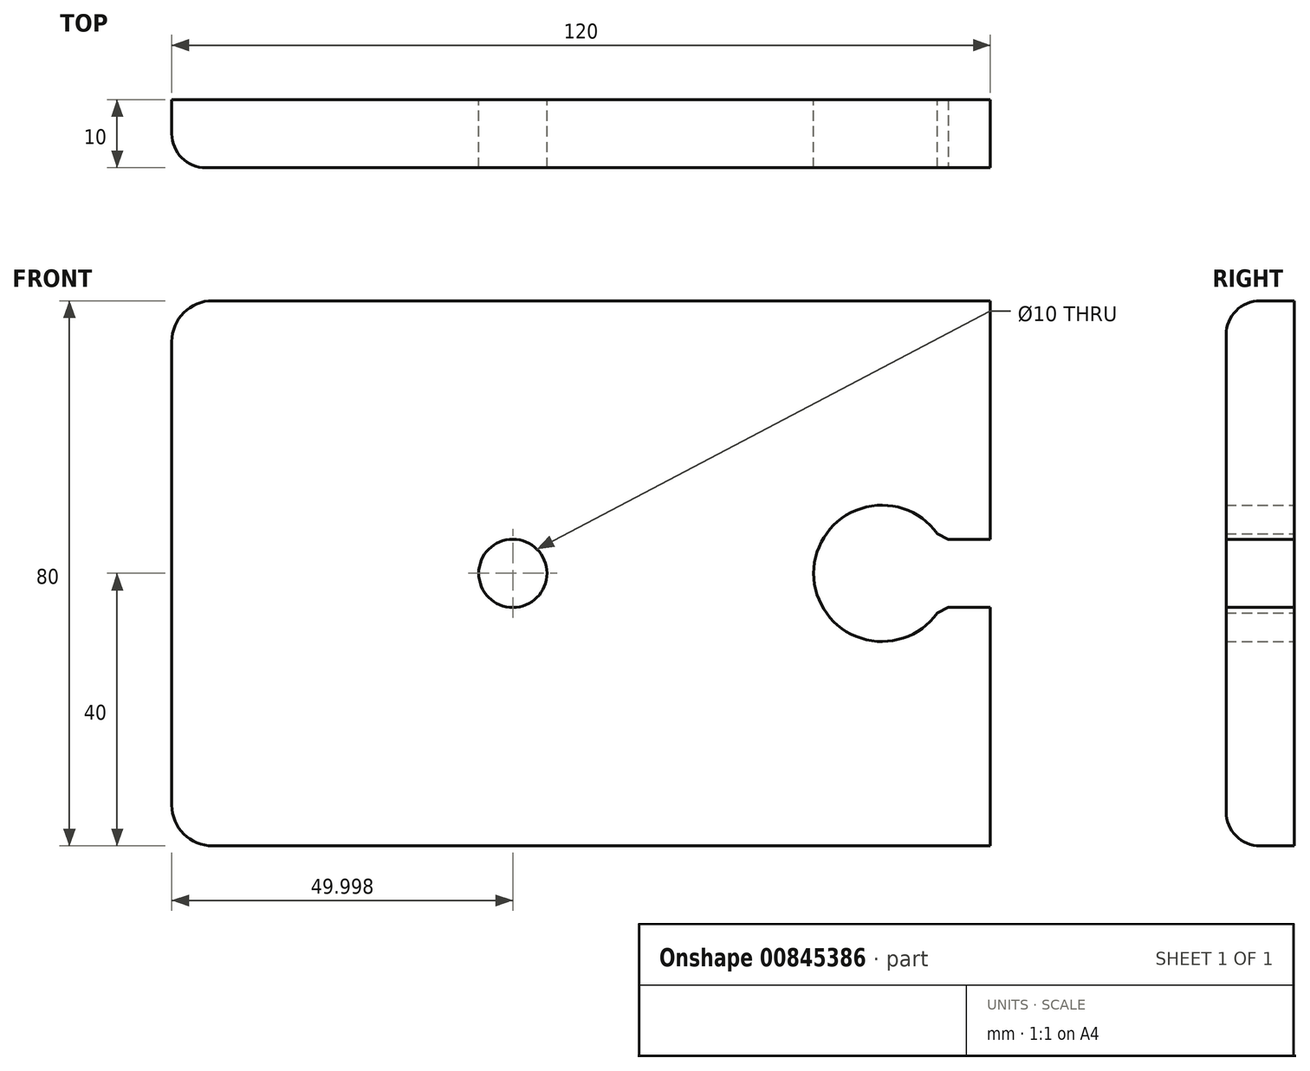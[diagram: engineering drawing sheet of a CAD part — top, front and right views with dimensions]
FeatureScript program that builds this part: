
annotation { "Feature Type Name" : "Feature", "Feature Type Description" : "" }
export const myFeature = defineFeature(function(context is Context, id is Id, definition is map)
    precondition{}
    {
        {
            var Q0;
            Q0=qCreatedBy(makeId("Front.planeOp"),FACE);
            var sketch = newSketch(context, id + "F0", { "sketchPlane" : qUnion([Q0])});
            skLineSegment(sketch, "E0.bottom", {"start": v(-66.83, 40) * mm, "end": v(53.17, 40) * mm});
            skLineSegment(sketch, "E0.top", {"start": v(-66.83, -40) * mm, "end": v(53.17, -40) * mm});
            skLineSegment(sketch, "E0.left", {"start": v(-66.83, 40) * mm, "end": v(-66.83, -40) * mm});
            skLineSegment(sketch, "E0.right", {"start": v(53.17, 40) * mm, "end": v(53.17, 5) * mm});
            skCircle(sketch, "E1", {"center": v(-16.83, 0) * mm, "radius": 5 * mm});
            skPoint(sketch, "E1.centerSnap0", {"position": v(-66.83, 0) * mm});
            skLineSegment(sketch, "E2.bottom", {"start": v(53.17, 5) * mm, "end": v(47.27, 5) * mm});
            skLineSegment(sketch, "E2.top", {"start": v(53.17, -5) * mm, "end": v(47.27, -5) * mm});
            skCircle(sketch, "E3", {"center": v(37.27, 0) * mm, "radius": 10 * mm});
            skPoint(sketch, "E3.centerSnap0", {"position": v(47.27, 0) * mm});
            skLineSegment(sketch, "E4", {"start": v(47.27, 5) * mm, "end": v(45.93, 5) * mm});
            skLineSegment(sketch, "E5", {"start": v(47.27, -5) * mm, "end": v(45.93, -5) * mm});
            skLineSegment(sketch, "E6.trimOffspring", {"start": v(53.17, -5) * mm, "end": v(53.17, -40) * mm});
            skSolve(sketch);
        }
        {
            var Q0;
            Q0=makeQuery(id+"F0.imprint","IMPRINT",FACE,{"disambiguationData":[TD([[makeQuery(id+"F0.imprint","IMPRINT",EDGE,{"derivedFrom":sQuery(id+"F0.wireOp",EDGE,"E0.bottom")}),-1.0]])]});
            extrude(context, id + "F1", {"entities" : qUnion([Q0]), "depth" : 10 * mm, "offsetDistance" : 25 * mm});
        }
        {
            var Q0;
            Q0=makeQuery(id+"F0.imprint","IMPRINT",FACE,{"disambiguationData":[TD([[makeQuery(id+"F0.imprint","IMPRINT",EDGE,{"derivedFrom":sQuery(id+"F0.wireOp",EDGE,"E1")}),1.0]])]});
            extrude(context, id + "F2", {"entities" : qUnion([Q0]), "operationType" : NewBodyOperationType.REMOVE, "oppositeDirection" : true, "depth" : 23.2 * mm, "offsetDistance" : 25 * mm});
        }
        {
            var Q0;
            Q0=makeQuery(id+"F1.opExtrude","SWEPT_EDGE",EDGE,{"disambiguationData":[OSD([sQuery(id+"F0.wireOp",EDGE,"E0.top"),sQuery(id+"F0.wireOp",EDGE,"E0.left")])]});
            var Q1;
            Q1=makeQuery(id+"F1.opExtrude","SWEPT_EDGE",EDGE,{"disambiguationData":[OSD([sQuery(id+"F0.wireOp",EDGE,"E0.bottom"),sQuery(id+"F0.wireOp",EDGE,"E0.left")])]});
            fillet(context, id + "F3", {"entities" : qUnion([Q0, Q1]), "radius" : 6 * mm, "tangentPropagation" : true, "allowEdgeOverflow" : false});
        }
        {
            var Q0;
            Q0=makeQuery(id+"F1.opExtrude","SWEPT_EDGE",EDGE,{"disambiguationData":[OSD([sQuery(id+"F0.wireOp",EDGE,"E3"),sQuery(id+"F0.wireOp",EDGE,"E5")])]});
            var Q1;
            Q1=makeQuery(id+"F1.opExtrude","SWEPT_EDGE",EDGE,{"disambiguationData":[OSD([sQuery(id+"F0.wireOp",EDGE,"E3"),sQuery(id+"F0.wireOp",EDGE,"E4")])]});
            chamfer(context, id + "F4", {"entities" : qUnion([Q0, Q1]), "width" : 2 * mm, "tangentPropagation" : true});
        }
        {
            var Q0;
            Q0=makeQuery(id+"F1.opExtrude","CAP_EDGE",EDGE,{"disambiguationData":[OSD([sQuery(id+"F0.wireOp",EDGE,"E0.top")])],"isStart":false});
            fillet(context, id + "F5", {"entities" : qUnion([Q0]), "radius" : 5 * mm, "tangentPropagation" : true, "allowEdgeOverflow" : false});
        }
    });
